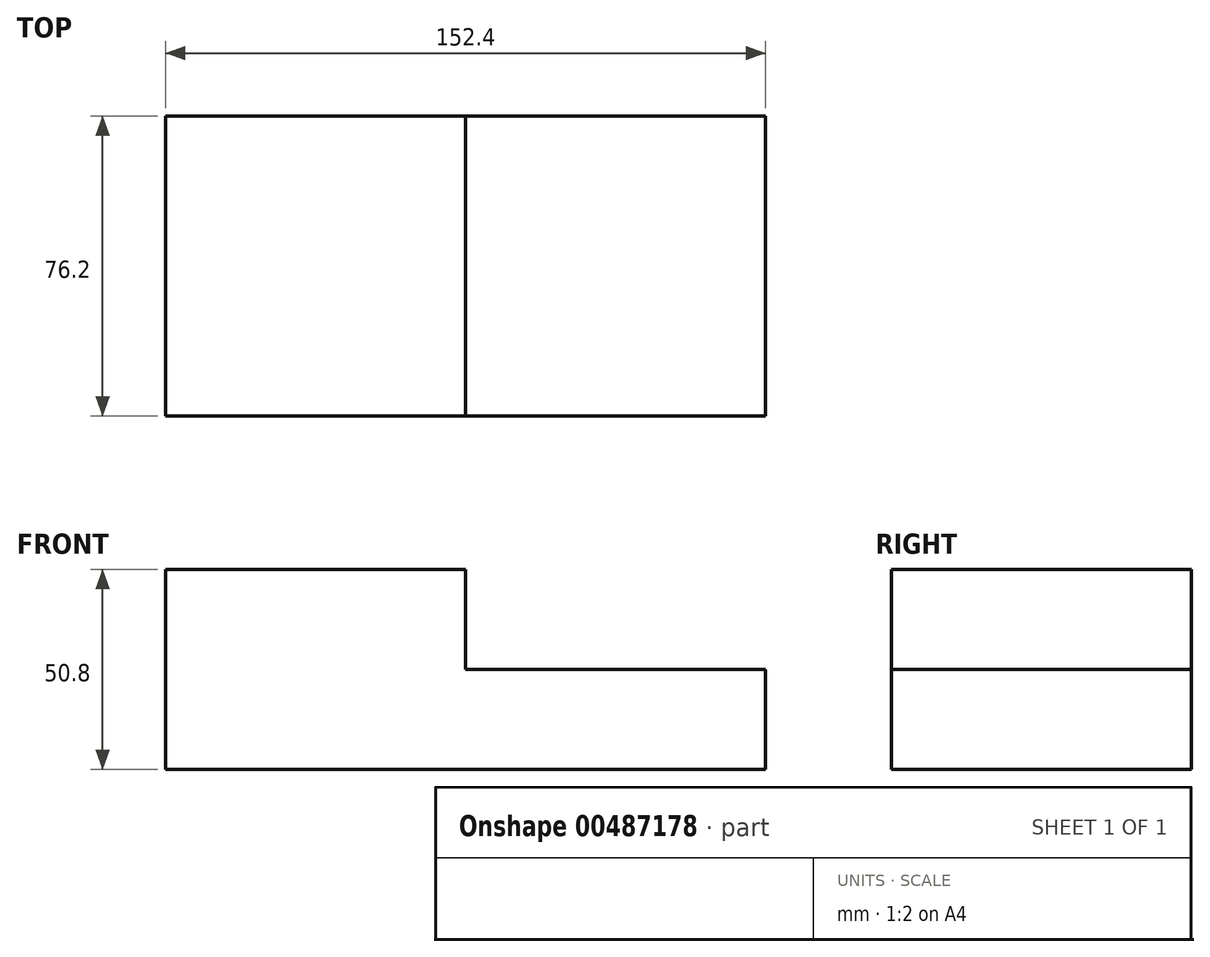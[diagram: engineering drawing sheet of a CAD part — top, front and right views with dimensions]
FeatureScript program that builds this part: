
annotation { "Feature Type Name" : "Feature", "Feature Type Description" : "" }
export const myFeature = defineFeature(function(context is Context, id is Id, definition is map)
    precondition{}
    {
        {
            var Q0;
            Q0=qCreatedBy(makeId("Front.planeOp"),FACE);
            var sketch = newSketch(context, id + "F0", { "sketchPlane" : qUnion([Q0])});
            skLineSegment(sketch, "E0", {"start": v(-105.96, 44.98) * mm, "end": v(-105.96, -5.82) * mm});
            skLineSegment(sketch, "E1", {"start": v(-105.96, 44.98) * mm, "end": v(-29.76, 44.98) * mm});
            skLineSegment(sketch, "E2", {"start": v(-29.76, 44.98) * mm, "end": v(-29.76, 19.58) * mm});
            skLineSegment(sketch, "E3", {"start": v(-29.76, 19.58) * mm, "end": v(46.44, 19.58) * mm});
            skLineSegment(sketch, "E4", {"start": v(-105.96, -5.82) * mm, "end": v(46.44, -5.82) * mm});
            skLineSegment(sketch, "E5", {"start": v(46.44, 19.58) * mm, "end": v(46.44, -5.82) * mm});
            skSolve(sketch);
        }
        {
            var Q0;
            Q0=makeQuery(id+"F0.imprint","IMPRINT",FACE,{"disambiguationData":[TD([[makeQuery(id+"F0.imprint","IMPRINT",EDGE,{"derivedFrom":sQuery(id+"F0.wireOp",EDGE,"E0")}),1.0]])]});
            extrude(context, id + "F1", {"entities" : qUnion([Q0]), "depth" : 76.2 * mm});
        }
    });
